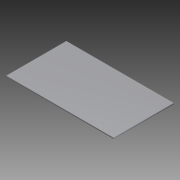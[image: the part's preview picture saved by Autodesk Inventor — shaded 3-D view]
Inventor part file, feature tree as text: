
AUTODESK INVENTOR PART (.ipt)
format: ipt  version: 2012 (Build 160160000, 160)  size: 81,920 bytes
history: native  units: in
note: dims shown in document units (in); Inventor stores cm internally (conversion verified against a paired STEP export)
features: extrude x2, sketch x2
ambient origin geometry x8: Origin, YZ Plane, XZ Plane, XY Plane, X Axis, Y Axis, Z Axis, Center Point
bodies: Solid1 (feature_tree)
feature tree (4):
  extrude  "Extrusion1"  Depth=0.25in
  extrude  "Extrusion2"  Depth=24.0in
  sketch  "Sketch1"  dims[d0=25.0in d1=0.25in]
  sketch  "Sketch2"  dims[d2=14.0in d3=0.0in d4=24.0in d5=14.0in d6=0.5in d7=14.0in d8=0.0in]
